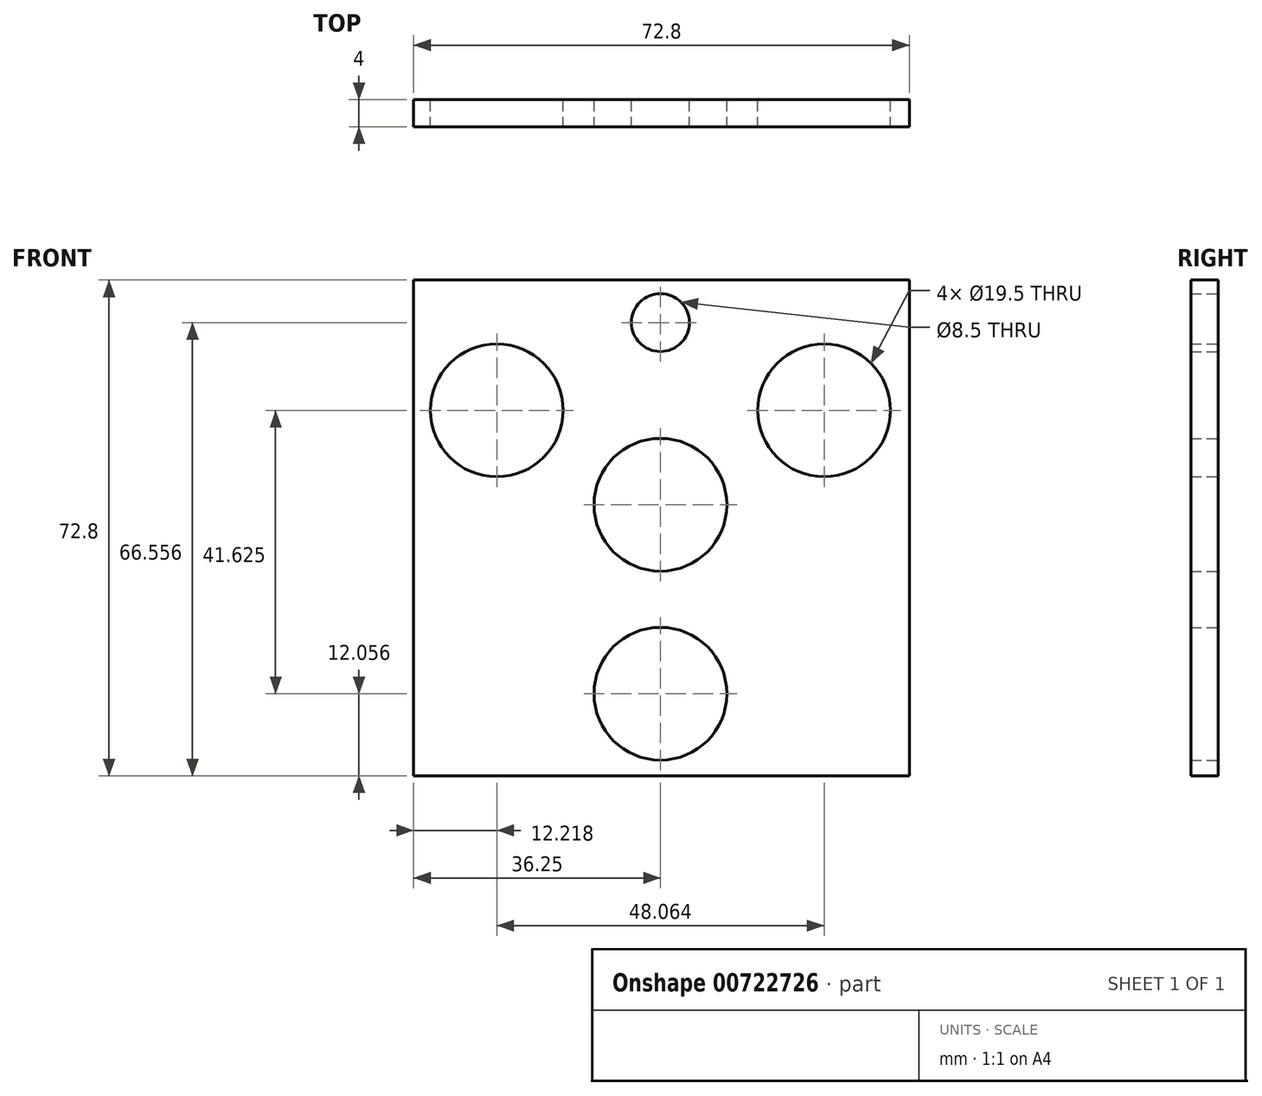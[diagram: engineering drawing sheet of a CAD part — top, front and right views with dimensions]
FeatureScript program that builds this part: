
annotation { "Feature Type Name" : "Feature", "Feature Type Description" : "" }
export const myFeature = defineFeature(function(context is Context, id is Id, definition is map)
    precondition{}
    {
        {
            var Q0;
            Q0=qCreatedBy(makeId("Front.planeOp"),FACE);
            var sketch = newSketch(context, id + "F0", { "sketchPlane" : qUnion([Q0])});
            skLineSegment(sketch, "E0.bottom", {"start": v(-40, 60) * mm, "end": v(40, 60) * mm});
            skLineSegment(sketch, "E0.top", {"start": v(-40, -60) * mm, "end": v(40, -60) * mm});
            skLineSegment(sketch, "E0.left", {"start": v(-40, 60) * mm, "end": v(-40, -60) * mm});
            skLineSegment(sketch, "E0.right", {"start": v(40, 60) * mm, "end": v(40, -60) * mm});
            skPoint(sketch, "E0.middle", {"position": v(0, 0) * mm});
            skLineSegment(sketch, "E1", {"start": v(0, 21.88) * mm, "end": v(0, 29.88) * mm, "construction": true});
            skCircle(sketch, "E2", {"center": v(0, 29.88) * mm, "radius": 8 * mm, "construction": true});
            skCircle(sketch, "E3", {"center": v(0, 29.88) * mm, "radius": 4.25 * mm});
            skLineSegment(sketch, "E4", {"start": v(0, 60) * mm, "end": v(0, 29.88) * mm, "construction": true});
            skLineSegment(sketch, "E5", {"start": v(0, 21.88) * mm, "end": v(0, 3.13) * mm, "construction": true});
            skCircle(sketch, "E6", {"center": v(0, 3.13) * mm, "radius": 18.75 * mm, "construction": true});
            skCircle(sketch, "E7.cCircle", {"center": v(0, 3.13) * mm, "radius": 27.75 * mm, "construction": true});
            skLineSegment(sketch, "E7.0", {"start": v(0, -24.62) * mm, "end": v(-24.03, 17) * mm, "construction": true});
            skLineSegment(sketch, "E7.1", {"start": v(-24.03, 17) * mm, "end": v(24.03, 17) * mm, "construction": true});
            skLineSegment(sketch, "E7.2", {"start": v(24.03, 17) * mm, "end": v(0, -24.62) * mm, "construction": true});
            skCircle(sketch, "E8", {"center": v(24.03, 17) * mm, "radius": 8 * mm, "construction": true});
            skCircle(sketch, "E9", {"center": v(-24.03, 17) * mm, "radius": 8 * mm, "construction": true});
            skCircle(sketch, "E10", {"center": v(0, -24.62) * mm, "radius": 8 * mm, "construction": true});
            skCircle(sketch, "E11", {"center": v(0, 3.13) * mm, "radius": 9.75 * mm});
            skCircle(sketch, "E12", {"center": v(24.03, 17) * mm, "radius": 9.75 * mm});
            skCircle(sketch, "E13", {"center": v(-24.03, 17) * mm, "radius": 9.75 * mm});
            skCircle(sketch, "E14", {"center": v(0, -24.62) * mm, "radius": 9.75 * mm});
            skSolve(sketch);
        }
        {
            var Q0;
            Q0=qSketchRegion(id+"F0",true);
            extrude(context, id + "F1", {"entities" : qUnion([Q0]), "depth" : 4 * mm, "offsetDistance" : 25 * mm});
        }
        {
            var Q0;
            Q0=makeQuery(id+"F1.opExtrude","CAP_FACE",FACE,{"disambiguationData":[OSD([sQuery(id+"F0.wireOp",EDGE,"E0.bottom"),sQuery(id+"F0.wireOp",EDGE,"E0.top"),sQuery(id+"F0.wireOp",EDGE,"E0.left"),sQuery(id+"F0.wireOp",EDGE,"E0.right"),sQuery(id+"F0.wireOp",EDGE,"E11"),sQuery(id+"F0.wireOp",EDGE,"E3"),sQuery(id+"F0.wireOp",EDGE,"E12"),sQuery(id+"F0.wireOp",EDGE,"E13"),sQuery(id+"F0.wireOp",EDGE,"E14")])],"isStart":false});
            var sketch = newSketch(context, id + "F3", { "sketchPlane" : qUnion([Q0])});
            skLineSegment(sketch, "E15.bottom", {"start": v(40, -60) * mm, "end": v(-40, -60) * mm});
            skLineSegment(sketch, "E15.top", {"start": v(40, -40) * mm, "end": v(-40, -40) * mm});
            skLineSegment(sketch, "E15.left", {"start": v(40, -60) * mm, "end": v(40, -40) * mm});
            skLineSegment(sketch, "E15.right", {"start": v(-40, -60) * mm, "end": v(-40, -40) * mm});
            skSolve(sketch);
        }
        {
            var Q0;
            Q0=qSketchRegion(id+"F3",true);
            extrude(context, id + "F4", {"entities" : qUnion([Q0]), "operationType" : NewBodyOperationType.REMOVE, "oppositeDirection" : true, "depth" : 10 * mm, "offsetDistance" : 25 * mm});
        }
        {
            var Q0;
            Q0=makeQuery(id+"F1.opExtrude","CAP_FACE",FACE,{"disambiguationData":[OSD([sQuery(id+"F0.wireOp",EDGE,"E0.bottom"),sQuery(id+"F0.wireOp",EDGE,"E0.top"),sQuery(id+"F0.wireOp",EDGE,"E0.left"),sQuery(id+"F0.wireOp",EDGE,"E0.right"),sQuery(id+"F0.wireOp",EDGE,"E11"),sQuery(id+"F0.wireOp",EDGE,"E3"),sQuery(id+"F0.wireOp",EDGE,"E12"),sQuery(id+"F0.wireOp",EDGE,"E13"),sQuery(id+"F0.wireOp",EDGE,"E14")])],"isStart":false});
            var sketch = newSketch(context, id + "F5", { "sketchPlane" : qUnion([Q0])});
            skLineSegment(sketch, "E16", {"start": v(0, 3.13) * mm, "end": v(42.5, 3.13) * mm, "construction": true});
            skLineSegment(sketch, "E17", {"start": v(42.5, 3.13) * mm, "end": v(42.5, 0.13) * mm, "construction": true});
            skLineSegment(sketch, "E18.bottom", {"start": v(40, 0) * mm, "end": v(46, 0) * mm});
            skLineSegment(sketch, "E18.top", {"start": v(40, 6) * mm, "end": v(46, 6) * mm});
            skLineSegment(sketch, "E18.left", {"start": v(40, 0) * mm, "end": v(40, 6) * mm});
            skLineSegment(sketch, "E18.right", {"start": v(46, 0) * mm, "end": v(46, 6) * mm});
            skCircle(sketch, "E19", {"center": v(42.5, 3.13) * mm, "radius": 0.95 * mm});
            skSolve(sketch);
        }
        {
            var Q0;
            Q0=qSketchRegion(id+"F5",true);
            extrude(context, id + "F6", {"entities" : qUnion([Q0]), "oppositeDirection" : true, "depth" : 10 * mm, "offsetDistance" : 25 * mm});
        }
        {
            var Q0;
            Q0=makeQuery(id+"F6.opExtrude","SWEPT_EDGE",EDGE,{"disambiguationData":[OSD([sQuery(id+"F5.wireOp",EDGE,"E18.bottom"),sQuery(id+"F5.wireOp",EDGE,"E18.right")])]});
            var Q1;
            Q1=makeQuery(id+"F6.opExtrude","SWEPT_EDGE",EDGE,{"disambiguationData":[OSD([sQuery(id+"F5.wireOp",EDGE,"E18.top"),sQuery(id+"F5.wireOp",EDGE,"E18.right")])]});
            fillet(context, id + "F7", {"entities" : qUnion([Q0, Q1]), "radius" : 3 * mm, "tangentPropagation" : true, "allowEdgeOverflow" : false});
        }
        {
            var Q0;
            Q0=makeQuery(id+"F6.opExtrude","SWEPT_BODY",BODY,{"disambiguationData":[OSD([sQuery(id+"F5.wireOp",EDGE,"E18.bottom"),sQuery(id+"F5.wireOp",EDGE,"E18.top"),sQuery(id+"F5.wireOp",EDGE,"E18.left"),sQuery(id+"F5.wireOp",EDGE,"E18.right"),sQuery(id+"F5.wireOp",EDGE,"E19")])]});
            var Q1;
            Q1=qCreatedBy(makeId("Right.planeOp"),FACE);
            mirror(context, id + "F8", {"operationType" : NewBodyOperationType.ADD, "entities" : qUnion([Q0]), "mirrorPlane" : qUnion([Q1])});
        }
        {
            var Q0;
            {var subQ0=makeQuery(id+"F6.opExtrude","CAP_FACE",FACE,{"disambiguationData":[OSD([sQuery(id+"F5.wireOp",EDGE,"E18.bottom"),sQuery(id+"F5.wireOp",EDGE,"E18.top"),sQuery(id+"F5.wireOp",EDGE,"E18.left"),sQuery(id+"F5.wireOp",EDGE,"E18.right"),sQuery(id+"F5.wireOp",EDGE,"E19")])],"isStart":true});Q0=makeQuery(id+"F8.boolean.opBoolean","MERGE",FACE,{"derivedFrom":[makeQuery(id+"F1.opExtrude","CAP_FACE",FACE,{"disambiguationData":[OSD([sQuery(id+"F0.wireOp",EDGE,"E0.bottom"),sQuery(id+"F0.wireOp",EDGE,"E0.top"),sQuery(id+"F0.wireOp",EDGE,"E0.left"),sQuery(id+"F0.wireOp",EDGE,"E0.right"),sQuery(id+"F0.wireOp",EDGE,"E11"),sQuery(id+"F0.wireOp",EDGE,"E3"),sQuery(id+"F0.wireOp",EDGE,"E12"),sQuery(id+"F0.wireOp",EDGE,"E13"),sQuery(id+"F0.wireOp",EDGE,"E14")])],"isStart":false}),subQ0,makeQuery(id+"F8.opPattern","COPY",FACE,{"derivedFrom":subQ0,"instanceName":"1"})]});}
            var sketch = newSketch(context, id + "F11", { "sketchPlane" : qUnion([Q0])});
            skLineSegment(sketch, "E20.bottom", {"start": v(-36.25, 36.12) * mm, "end": v(36.55, 36.12) * mm});
            skLineSegment(sketch, "E20.top", {"start": v(-36.25, -36.68) * mm, "end": v(36.55, -36.68) * mm});
            skLineSegment(sketch, "E20.left", {"start": v(-36.25, 36.12) * mm, "end": v(-36.25, -36.68) * mm});
            skLineSegment(sketch, "E20.right", {"start": v(36.55, 36.12) * mm, "end": v(36.55, -36.68) * mm});
            skLineSegment(sketch, "E21.bottom", {"start": v(-47.82, 62.45) * mm, "end": v(50.12, 62.45) * mm});
            skLineSegment(sketch, "E21.top", {"start": v(-47.82, -65.4) * mm, "end": v(50.12, -65.4) * mm});
            skLineSegment(sketch, "E21.left", {"start": v(-47.82, 62.45) * mm, "end": v(-47.82, -65.4) * mm});
            skLineSegment(sketch, "E21.right", {"start": v(50.12, 62.45) * mm, "end": v(50.12, -65.4) * mm});
            skSolve(sketch);
        }
        {
            var Q0;
            Q0 = qSketchRegion(id + "F11", true);
            extrude(context, id + "F12", {"entities" : qUnion([Q0]), "operationType" : NewBodyOperationType.REMOVE, "oppositeDirection" : true, "depth" : 10 * mm, "offsetDistance" : 25 * mm});
        }
    });
